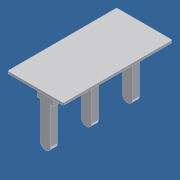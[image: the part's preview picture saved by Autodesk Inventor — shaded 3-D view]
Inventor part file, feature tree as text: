
AUTODESK INVENTOR PART (.ipt)
format: ipt  version: 2014 (Build 180170000, 170)  size: 115,712 bytes
history: native  units: in
note: dims shown in document units (in); Inventor stores cm internally (conversion verified against a paired STEP export)
features: other x7, extrude x2, sketch x2, pattern_linear x1
ambient origin geometry x8: Origin, YZ Plane, XZ Plane, XY Plane, X Axis, Y Axis, Z Axis, Center Point
bodies: Solid1 (feature_tree)
feature tree (12):
  extrude  "Extrusion1"  Depth=0.031in TaperAngle=0.0deg
  extrude  "Extrusion2"  [1 undecoded]
  pattern_linear  "Rectangular Pattern1"  [2 undecoded]
  other  "to_base_XY"
  other  "to_base_YZ"
  other  "to_base_ZX"
  other  "to_base_X"
  other  "to_base_Y"
  other  "to_base_Z"
  other  "to_base_Center"
  sketch  "Sketch_2"  dims[d0=0.01in d1=0.0in d2=0.031in d3=0.0in]
  sketch  "Sketch_7"  dims[d4=1.1811in d6=0.185in d7=0.3937in d9=0.0in]
note: 3 required parameter values undecoded (feature->parameter linkage not recoverable at this tier; creation-order binding heuristic only, values carry confidence <= 0.55)
